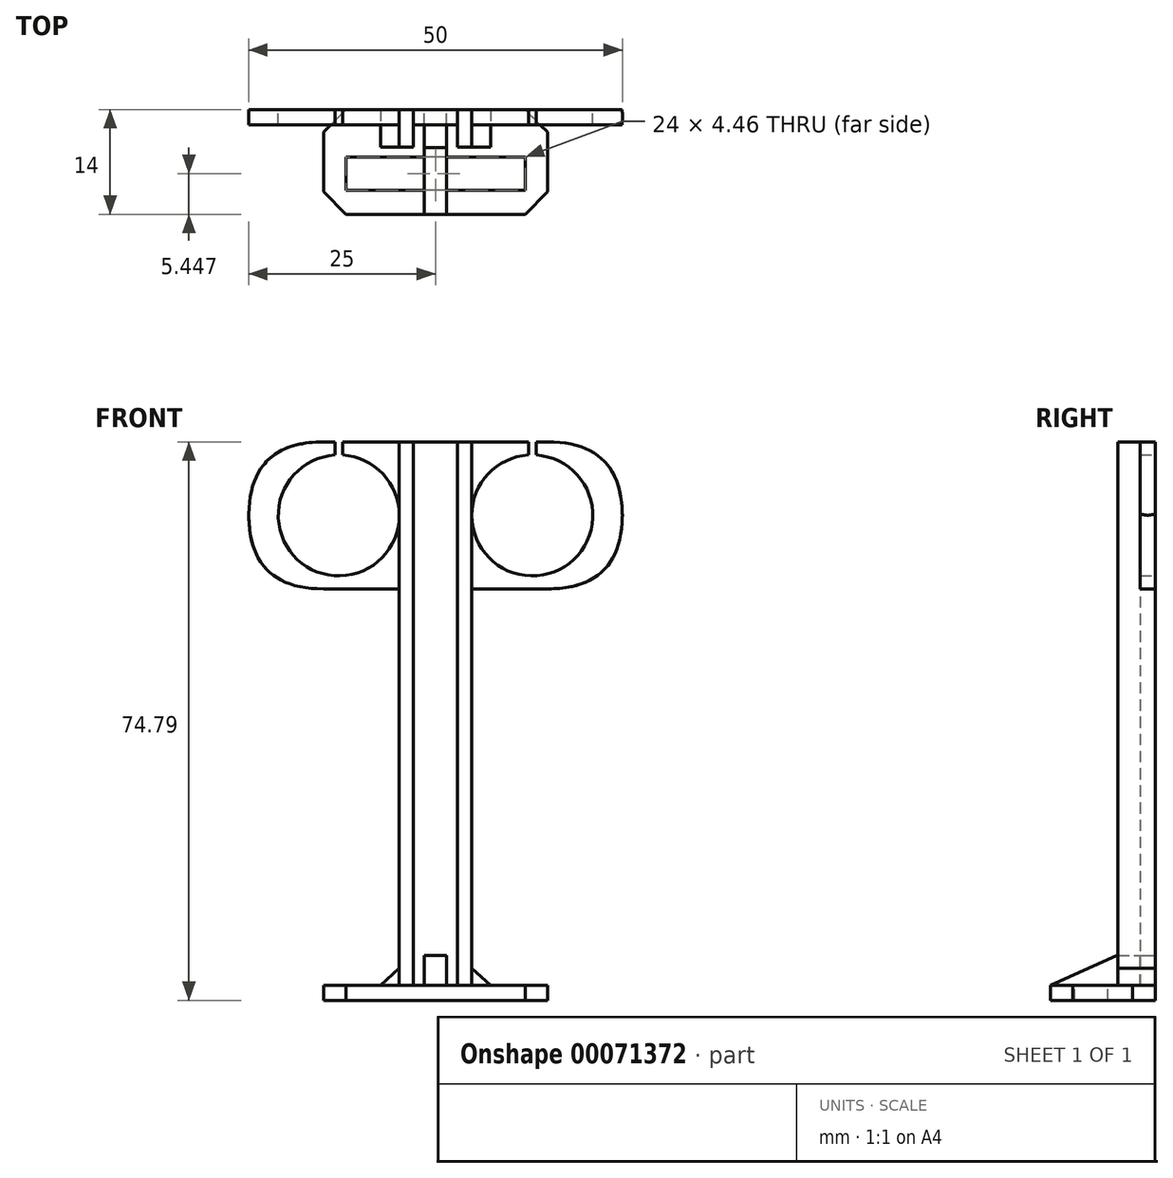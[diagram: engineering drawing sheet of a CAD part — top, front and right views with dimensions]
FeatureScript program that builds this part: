
annotation { "Feature Type Name" : "Feature", "Feature Type Description" : "" }
export const myFeature = defineFeature(function(context is Context, id is Id, definition is map)
    precondition{}
    {
        {
            var Q0;
            Q0=qCreatedBy(makeId("Front.planeOp"),FACE);
            var sketch = newSketch(context, id + "F0", { "sketchPlane" : qUnion([Q0])});
            skLineSegment(sketch, "E0.bottom", {"start": v(25, 53.99) * mm, "end": v(-25, 53.99) * mm});
            skLineSegment(sketch, "E0.top", {"start": v(25, 34.3) * mm, "end": v(-25, 34.3) * mm});
            skLineSegment(sketch, "E0.left", {"start": v(25, 53.99) * mm, "end": v(25, 34.3) * mm});
            skLineSegment(sketch, "E0.right", {"start": v(-25, 53.99) * mm, "end": v(-25, 34.3) * mm});
            skPoint(sketch, "E0.middle", {"position": v(0, 44.15) * mm});
            skCircle(sketch, "E1", {"center": v(-12.95, 44.15) * mm, "radius": 8.1 * mm});
            skLineSegment(sketch, "E2", {"start": v(0, 53.99) * mm, "end": v(0, 34.3) * mm, "construction": true});
            skCircle(sketch, "E3.MirrorC", {"center": v(12.95, 44.15) * mm, "radius": 8.1 * mm});
            skLineSegment(sketch, "E4", {"start": v(-12.95, 53.99) * mm, "end": v(-12.95, 34.3) * mm});
            skLineSegment(sketch, "E5", {"start": v(12.95, 53.99) * mm, "end": v(12.95, 34.3) * mm});
            skLineSegment(sketch, "E6", {"start": v(-13.45, 52.23) * mm, "end": v(-13.45, 53.99) * mm});
            skLineSegment(sketch, "E7", {"start": v(-12.45, 52.23) * mm, "end": v(-12.45, 53.99) * mm});
            skLineSegment(sketch, "E8.MirrorCS", {"start": v(13.45, 52.23) * mm, "end": v(13.45, 53.99) * mm});
            skLineSegment(sketch, "E9.MirrorCS", {"start": v(12.45, 52.23) * mm, "end": v(12.45, 53.99) * mm});
            skLineSegment(sketch, "E10", {"start": v(-12.95, 44.15) * mm, "end": v(-4.85, 44.15) * mm});
            skLineSegment(sketch, "E11", {"start": v(12.95, 44.15) * mm, "end": v(4.85, 44.15) * mm});
            skLineSegment(sketch, "E12", {"start": v(-4.85, 53.99) * mm, "end": v(-4.85, -18.8) * mm});
            skLineSegment(sketch, "E13.MirrorCS", {"start": v(4.85, 53.99) * mm, "end": v(4.85, -18.8) * mm});
            skLineSegment(sketch, "E14", {"start": v(-2.95, 53.99) * mm, "end": v(-2.95, -18.8) * mm});
            skLineSegment(sketch, "E15", {"start": v(-4.85, -18.8) * mm, "end": v(4.85, -18.8) * mm});
            skLineSegment(sketch, "E16.MirrorCS", {"start": v(2.95, 53.99) * mm, "end": v(2.95, -18.8) * mm});
            skLineSegment(sketch, "E17", {"start": v(-1.5, -18.8) * mm, "end": v(-1.5, -14.8) * mm});
            skLineSegment(sketch, "E18", {"start": v(-1.5, -14.8) * mm, "end": v(0, -14.8) * mm});
            skLineSegment(sketch, "E19", {"start": v(0, -14.8) * mm, "end": v(0, -18.8) * mm});
            skLineSegment(sketch, "E20.MirrorCS", {"start": v(1.5, -14.8) * mm, "end": v(0, -14.8) * mm});
            skLineSegment(sketch, "E21.MirrorCS", {"start": v(1.5, -18.8) * mm, "end": v(1.5, -14.8) * mm});
            skSolve(sketch);
        }
        {
            var Q0;
            {var subQ0=sQuery(id+"F0.wireOp",EDGE,"E0.right");Q0=makeQuery(id+"F0.imprint","IMPRINT",FACE,{"disambiguationData":[TD([[makeQuery(id+"F0.imprint","IMPRINT",EDGE,{"derivedFrom":subQ0}),1.0]])]});}
            var Q1;
            {var subQ0=sQuery(id+"F0.wireOp",EDGE,"E4");var subQ1=sQuery(id+"F0.wireOp",EDGE,"E0.top");var subQ2=makeQuery(id+"F0.imprint","INTERSECT",VERTEX,{"derivedFrom":[subQ1,subQ0]});Q1=makeQuery(id+"F0.imprint","IMPRINT",FACE,{"disambiguationData":[TD([[makeQuery(id+"F0.imprint","IMPRINT",EDGE,{"disambiguationData":[TD([[subQ2,1.0]])],"derivedFrom":subQ1}),-1.0]])]});}
            var Q2;
            {var subQ0=sQuery(id+"F0.wireOp",EDGE,"E7");Q2=makeQuery(id+"F0.imprint","IMPRINT",FACE,{"disambiguationData":[TD([[makeQuery(id+"F0.imprint","IMPRINT",EDGE,{"derivedFrom":subQ0}),-1.0]])]});}
            var Q3;
            {var subQ0=sQuery(id+"F0.wireOp",EDGE,"E9.MirrorCS");Q3=makeQuery(id+"F0.imprint","IMPRINT",FACE,{"disambiguationData":[TD([[makeQuery(id+"F0.imprint","IMPRINT",EDGE,{"derivedFrom":subQ0}),1.0]])]});}
            var Q4;
            {var subQ0=sQuery(id+"F0.wireOp",EDGE,"E5");var subQ1=sQuery(id+"F0.wireOp",EDGE,"E0.top");var subQ2=makeQuery(id+"F0.imprint","INTERSECT",VERTEX,{"derivedFrom":[subQ1,subQ0]});Q4=makeQuery(id+"F0.imprint","IMPRINT",FACE,{"disambiguationData":[TD([[makeQuery(id+"F0.imprint","IMPRINT",EDGE,{"disambiguationData":[TD([[subQ2,-1.0]])],"derivedFrom":subQ1}),-1.0]])]});}
            var Q5;
            {var subQ4=sQuery(id+"F0.wireOp",EDGE,"E0.left");Q5=makeQuery(id+"F0.imprint","IMPRINT",FACE,{"disambiguationData":[TD([[makeQuery(id+"F0.imprint","IMPRINT",EDGE,{"derivedFrom":subQ4}),-1.0]])]});}
            var Q6;
            {var subQ0=sQuery(id+"F0.wireOp",EDGE,"E14");var subQ1=sQuery(id+"F0.wireOp",EDGE,"E0.bottom");var subQ2=makeQuery(id+"F0.imprint","INTERSECT",VERTEX,{"derivedFrom":[subQ1,subQ0]});Q6=makeQuery(id+"F0.imprint","IMPRINT",FACE,{"disambiguationData":[TD([[makeQuery(id+"F0.imprint","IMPRINT",EDGE,{"disambiguationData":[TD([[subQ2,1.0]])],"derivedFrom":subQ1}),1.0]])]});}
            var Q7;
            {var subQ0=sQuery(id+"F0.wireOp",EDGE,"E16.MirrorCS");var subQ1=sQuery(id+"F0.wireOp",EDGE,"E0.top");var subQ2=makeQuery(id+"F0.imprint","INTERSECT",VERTEX,{"derivedFrom":[subQ1,subQ0]});Q7=makeQuery(id+"F0.imprint","IMPRINT",FACE,{"disambiguationData":[TD([[makeQuery(id+"F0.imprint","IMPRINT",EDGE,{"disambiguationData":[TD([[subQ2,-1.0]])],"derivedFrom":subQ1}),1.0]])]});}
            extrude(context, id + "F1", {"entities" : qUnion([Q0, Q1, Q2, Q3, Q4, Q5, Q6, Q7]), "depth" : 2 * mm});
        }
        {
            var Q0;
            {var subQ0=sQuery(id+"F0.wireOp",EDGE,"E12");var subQ1=sQuery(id+"F0.wireOp",EDGE,"E0.top");var subQ2=makeQuery(id+"F0.imprint","INTERSECT",VERTEX,{"derivedFrom":[subQ1,subQ0]});Q0=makeQuery(id+"F0.imprint","IMPRINT",FACE,{"disambiguationData":[TD([[makeQuery(id+"F0.imprint","IMPRINT",EDGE,{"disambiguationData":[TD([[subQ2,1.0]])],"derivedFrom":subQ1}),1.0]])]});}
            var Q1;
            {var subQ0=sQuery(id+"F0.wireOp",EDGE,"E12");var subQ4=sQuery(id+"F0.wireOp",EDGE,"E0.bottom");var subQ5=makeQuery(id+"F0.imprint","INTERSECT",VERTEX,{"derivedFrom":[subQ4,subQ0]});Q1=makeQuery(id+"F0.imprint","IMPRINT",FACE,{"disambiguationData":[TD([[makeQuery(id+"F0.imprint","IMPRINT",EDGE,{"disambiguationData":[TD([[subQ5,1.0]])],"derivedFrom":subQ4}),1.0]])]});}
            var Q2;
            {var subQ0=sQuery(id+"F0.wireOp",EDGE,"E13.MirrorCS");var subQ1=sQuery(id+"F0.wireOp",EDGE,"E0.top");var subQ2=makeQuery(id+"F0.imprint","INTERSECT",VERTEX,{"derivedFrom":[subQ1,subQ0]});Q2=makeQuery(id+"F0.imprint","IMPRINT",FACE,{"disambiguationData":[TD([[makeQuery(id+"F0.imprint","IMPRINT",EDGE,{"disambiguationData":[TD([[subQ2,-1.0]])],"derivedFrom":subQ1}),1.0]])]});}
            var Q3;
            {var subQ0=sQuery(id+"F0.wireOp",EDGE,"E13.MirrorCS");var subQ6=sQuery(id+"F0.wireOp",EDGE,"E0.bottom");var subQ7=makeQuery(id+"F0.imprint","INTERSECT",VERTEX,{"derivedFrom":[subQ6,subQ0]});Q3=makeQuery(id+"F0.imprint","IMPRINT",FACE,{"disambiguationData":[TD([[makeQuery(id+"F0.imprint","IMPRINT",EDGE,{"disambiguationData":[TD([[subQ7,-1.0]])],"derivedFrom":subQ6}),1.0]])]});}
            extrude(context, id + "F2", {"entities" : qUnion([Q0, Q1, Q2, Q3]), "depth" : 5 * mm});
        }
        {
            var Q0;
            Q0=makeQuery(id+"F1.opExtrude","SWEPT_EDGE",EDGE,{"disambiguationData":[OSD([sQuery(id+"F0.wireOp",EDGE,"E0.bottom"),sQuery(id+"F0.wireOp",EDGE,"E0.right")])]});
            var Q1;
            Q1=makeQuery(id+"F1.opExtrude","SWEPT_EDGE",EDGE,{"disambiguationData":[OSD([sQuery(id+"F0.wireOp",EDGE,"E0.top"),sQuery(id+"F0.wireOp",EDGE,"E0.right")])]});
            var Q2;
            Q2=makeQuery(id+"F1.opExtrude","SWEPT_EDGE",EDGE,{"disambiguationData":[OSD([sQuery(id+"F0.wireOp",EDGE,"E0.top"),sQuery(id+"F0.wireOp",EDGE,"E0.left")])]});
            var Q3;
            Q3=makeQuery(id+"F1.opExtrude","SWEPT_EDGE",EDGE,{"disambiguationData":[OSD([sQuery(id+"F0.wireOp",EDGE,"E0.bottom"),sQuery(id+"F0.wireOp",EDGE,"E0.left")])]});
            fillet(context, id + "F3", {"entities" : qUnion([Q0, Q1, Q2, Q3]), "radius" : 10 * mm, "tangentPropagation" : true, "rho" : 0.5, "crossSection" : FilletCrossSection.CONIC, "allowEdgeOverflow" : false});
        }
        {
            var Q0;
            Q0=makeQuery(id+"F1.opExtrude","SWEPT_FACE",FACE,{"disambiguationData":[OSD([sQuery(id+"F0.wireOp",EDGE,"E15")])]});
            var sketch = newSketch(context, id + "F4", { "sketchPlane" : qUnion([Q0])});
            skPoint(sketch, "E22.endSnap0", {"position": v(-2.22, 0) * mm});
            skLineSegment(sketch, "E23", {"start": v(-15, 0) * mm, "end": v(-15, 14) * mm});
            skLineSegment(sketch, "E24", {"start": v(-15, 14) * mm, "end": v(15, 14) * mm});
            skLineSegment(sketch, "E25", {"start": v(15, 14) * mm, "end": v(15, 0) * mm});
            skPoint(sketch, "E26.middle", {"position": v(-2.22, 8.5) * mm});
            skPoint(sketch, "E27", {"position": v(0, 8.55) * mm});
            skLineSegment(sketch, "E28", {"start": v(0, 0) * mm, "end": v(-15, 0) * mm});
            skLineSegment(sketch, "E29", {"start": v(0, 0) * mm, "end": v(15, 0) * mm});
            skLineSegment(sketch, "E30.bottom", {"start": v(12, 6.32) * mm, "end": v(-12, 6.32) * mm});
            skLineSegment(sketch, "E30.top", {"start": v(12, 10.78) * mm, "end": v(-12, 10.78) * mm});
            skLineSegment(sketch, "E30.left", {"start": v(12, 6.32) * mm, "end": v(12, 10.78) * mm});
            skLineSegment(sketch, "E30.right", {"start": v(-12, 6.32) * mm, "end": v(-12, 10.78) * mm});
            skSolve(sketch);
        }
        {
            var Q0;
            {var subQ3=sQuery(id+"F4.wireOp",EDGE,"E23");Q0=makeQuery(id+"F4.imprint","IMPRINT",FACE,{"disambiguationData":[TD([[makeQuery(id+"F4.imprint","IMPRINT",EDGE,{"derivedFrom":subQ3}),-1.0]])]});}
            var Q1;
            {var subQ0=sQuery(id+"F0.wireOp",EDGE,"E15");Q1=makeQuery(id+"F4.imprint","IMPRINT",FACE,{"disambiguationData":[TD([[makeQuery(id+"F4.imprint","IMPRINT",EDGE,{"derivedFrom":makeQuery(id+"F1.opExtrude","CAP_EDGE",EDGE,{"disambiguationData":[OSD([subQ0])],"isStart":false})}),-1.0]])]});}
            extrude(context, id + "F5", {"entities" : qUnion([Q0, Q1]), "depth" : 2 * mm});
        }
        {
            var Q0;
            Q0=makeQuery(id+"F5.opExtrude","SWEPT_EDGE",EDGE,{"disambiguationData":[OSD([sQuery(id+"F4.wireOp",EDGE,"a5WS0ALz-HKaF-vjAs-BoWF-bQespx2GAHpp"),sQuery(id+"F4.wireOp",EDGE,"E23")])]});
            var Q1;
            Q1=makeQuery(id+"F5.opExtrude","SWEPT_EDGE",EDGE,{"disambiguationData":[OSD([sQuery(id+"F4.wireOp",EDGE,"E23"),sQuery(id+"F4.wireOp",EDGE,"E24")])]});
            var Q2;
            Q2=makeQuery(id+"F5.opExtrude","SWEPT_EDGE",EDGE,{"disambiguationData":[OSD([sQuery(id+"F4.wireOp",EDGE,"E24"),sQuery(id+"F4.wireOp",EDGE,"E25")])]});
            var Q3;
            Q3=makeQuery(id+"F5.opExtrude","SWEPT_EDGE",EDGE,{"disambiguationData":[OSD([sQuery(id+"F4.wireOp",EDGE,"E22"),sQuery(id+"F4.wireOp",EDGE,"E25")])]});
            chamfer(context, id + "F6", {"entities" : qUnion([Q0, Q1, Q2, Q3]), "width" : 3 * mm, "tangentPropagation" : true});
        }
        {
            var Q0;
            Q0=makeQuery(id+"F2.opExtrude","CAP_FACE",FACE,{"disambiguationData":[OSD([sQuery(id+"F0.wireOp",EDGE,"E0.bottom"),sQuery(id+"F0.wireOp",EDGE,"E13.MirrorCS"),sQuery(id+"F0.wireOp",EDGE,"E15"),sQuery(id+"F0.wireOp",EDGE,"E16.MirrorCS")])],"isStart":false});
            var sketch = newSketch(context, id + "F7", { "sketchPlane" : qUnion([Q0])});
            skLineSegment(sketch, "E31", {"start": v(0, 0) * mm, "end": v(0, -18.68) * mm});
            skPoint(sketch, "E32.endSnap0", {"position": v(3.9, -18.8) * mm});
            skLineSegment(sketch, "E33", {"start": v(4.85, -16.5) * mm, "end": v(7.38, -18.8) * mm});
            skLineSegment(sketch, "E34", {"start": v(2.95, -18.8) * mm, "end": v(7.38, -18.8) * mm});
            skLineSegment(sketch, "E35", {"start": v(7.38, -18.8) * mm, "end": v(8.83, -18.8) * mm});
            skLineSegment(sketch, "E36.MirrorCS", {"start": v(-4.85, -16.5) * mm, "end": v(-7.38, -18.8) * mm});
            skLineSegment(sketch, "E37", {"start": v(-4.85, -16.5) * mm, "end": v(-4.85, -18.8) * mm});
            skLineSegment(sketch, "E38", {"start": v(-4.85, -18.8) * mm, "end": v(-7.38, -18.8) * mm});
            skSolve(sketch);
        }
        {
            var Q0;
            Q0 = qSketchRegion(id + "F7", true);
            var Q1;
            {var subQ0=sQuery(id+"F7.wireOp",EDGE,"E33");Q1=makeQuery(id+"F7.imprint","IMPRINT",FACE,{"disambiguationData":[TD([[makeQuery(id+"F7.imprint","IMPRINT",EDGE,{"derivedFrom":subQ0}),-1.0]])]});}
            extrude(context, id + "F8", {"entities" : qUnion([Q0, Q1]), "oppositeDirection" : true, "depth" : 5 * mm});
        }
        {
            var Q0;
            {var subQ0=sQuery(id+"F0.wireOp",EDGE,"E19");Q0=makeQuery(id+"F0.imprint","IMPRINT",FACE,{"disambiguationData":[TD([[makeQuery(id+"F0.imprint","IMPRINT",EDGE,{"derivedFrom":subQ0}),1.0]])]});}
            var Q1;
            {var subQ0=sQuery(id+"F0.wireOp",EDGE,"E17");Q1=makeQuery(id+"F0.imprint","IMPRINT",FACE,{"disambiguationData":[TD([[makeQuery(id+"F0.imprint","IMPRINT",EDGE,{"derivedFrom":subQ0}),-1.0]])]});}
            extrude(context, id + "F9", {"entities" : qUnion([Q0, Q1]), "depth" : 14 * mm});
        }
        {
            var Q0;
            Q0=makeQuery(id+"F9.opExtrude","SWEPT_FACE",FACE,{"disambiguationData":[OSD([sQuery(id+"F0.wireOp",EDGE,"E17")])]});
            var sketch = newSketch(context, id + "F10", { "sketchPlane" : qUnion([Q0])});
            skLineSegment(sketch, "E39", {"start": v(14, -18.8) * mm, "end": v(5.1, -14.8) * mm});
            skLineSegment(sketch, "E40", {"start": v(5.1, -14.8) * mm, "end": v(5.1, -18.8) * mm});
            skLineSegment(sketch, "E41", {"start": v(5.1, -18.8) * mm, "end": v(14, -18.8) * mm});
            skLineSegment(sketch, "E42", {"start": v(5.1, -14.8) * mm, "end": v(14, -14.8) * mm});
            skLineSegment(sketch, "E43", {"start": v(14, -14.8) * mm, "end": v(14, -18.8) * mm});
            skSolve(sketch);
        }
        {
            var Q0;
            Q0=makeQuery(id+"F10.imprint","IMPRINT",FACE,{"disambiguationData":[TD([[makeQuery(id+"F10.imprint","IMPRINT",EDGE,{"derivedFrom":sQuery(id+"F10.wireOp",EDGE,"E39")}),-1.0]])]});
            extrude(context, id + "F11", {"entities" : qUnion([Q0]), "operationType" : NewBodyOperationType.REMOVE, "oppositeDirection" : true, "depth" : 3 * mm});
        }
    });
